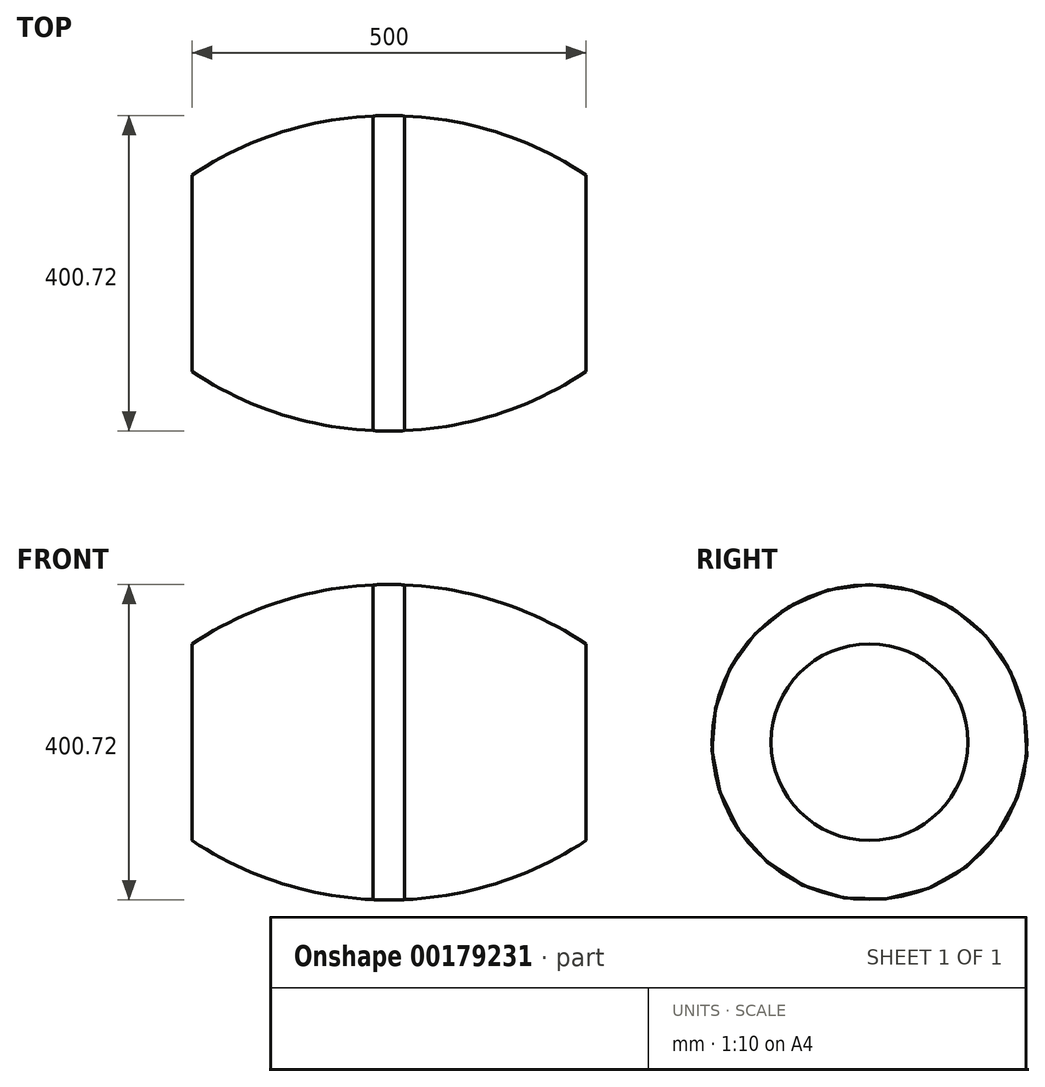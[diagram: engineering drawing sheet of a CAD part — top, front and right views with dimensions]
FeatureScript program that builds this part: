
annotation { "Feature Type Name" : "Feature", "Feature Type Description" : "" }
export const myFeature = defineFeature(function(context is Context, id is Id, definition is map)
    precondition{}
    {
        {
            var Q0;
            Q0=qCreatedBy(makeId("Front.planeOp"),FACE);
            var sketch = newSketch(context, id + "F0", { "sketchPlane" : qUnion([Q0])});
            skLineSegment(sketch, "E0", {"start": v(0, 0) * mm, "end": v(500, 0) * mm, "construction": true});
            skLineSegment(sketch, "E1", {"start": v(0, 0) * mm, "end": v(0, 125) * mm, "construction": true});
            skLineSegment(sketch, "E2", {"start": v(250, 0) * mm, "end": v(250, 200) * mm, "construction": true});
            skLineSegment(sketch, "E3", {"start": v(500, 0) * mm, "end": v(500, 125) * mm, "construction": true});
            skArc(sketch, "E4", {"start": v(500, 125) * mm, "mid": v(250, 200.36) * mm, "end": v(0, 125) * mm});
            skLineSegment(sketch, "E5", {"start": v(0, 125) * mm, "end": v(0, 0) * mm});
            skLineSegment(sketch, "E6", {"start": v(500, 125) * mm, "end": v(500, 0) * mm});
            skLineSegment(sketch, "E7", {"start": v(0, 0) * mm, "end": v(500, 0) * mm});
            skLineSegment(sketch, "E8", {"start": v(250, 0) * mm, "end": v(250, 200) * mm});
            skLineSegment(sketch, "E9", {"start": v(250, 0) * mm, "end": v(230, 0) * mm, "construction": true});
            skLineSegment(sketch, "E10", {"start": v(250, 0) * mm, "end": v(270, 0) * mm});
            skLineSegment(sketch, "E11", {"start": v(230, 0) * mm, "end": v(230, 199.92) * mm});
            skLineSegment(sketch, "E12", {"start": v(270, 0) * mm, "end": v(270, 199.92) * mm});
            skArc(sketch, "E13", {"start": v(270, 199.92) * mm, "mid": v(250, 200.17) * mm, "end": v(230, 199.92) * mm});
            skSolve(sketch);
        }
        {
            var Q0;
            Q0=makeQuery(id+"F0.imprint","IMPRINT",FACE,{"disambiguationData":[TD([[makeQuery(id+"F0.imprint","IMPRINT",EDGE,{"derivedFrom":sQuery(id+"F0.wireOp",EDGE,"E4")}),1.0]])]});
            var Q1;
            {var subQ0=sQuery(id+"F0.wireOp",EDGE,"E5");Q1=makeQuery(id+"F0.imprint","IMPRINT",FACE,{"disambiguationData":[TD([[makeQuery(id+"F0.imprint","IMPRINT",EDGE,{"derivedFrom":subQ0}),1.0]])]});}
            var Q2;
            {var subQ0=sQuery(id+"F0.wireOp",EDGE,"E6");Q2=makeQuery(id+"F0.imprint","IMPRINT",FACE,{"disambiguationData":[TD([[makeQuery(id+"F0.imprint","IMPRINT",EDGE,{"derivedFrom":subQ0}),-1.0]])]});}
            var Q3;
            Q3=sQuery(id+"F0.wireOp",EDGE,"E7");
            revolve(context, id + "F1", {"entities" : qUnion([Q0, Q1, Q2]), "axis" : qUnion([Q3]), "revolveType" : RevolveType.FULL});
        }
    });
